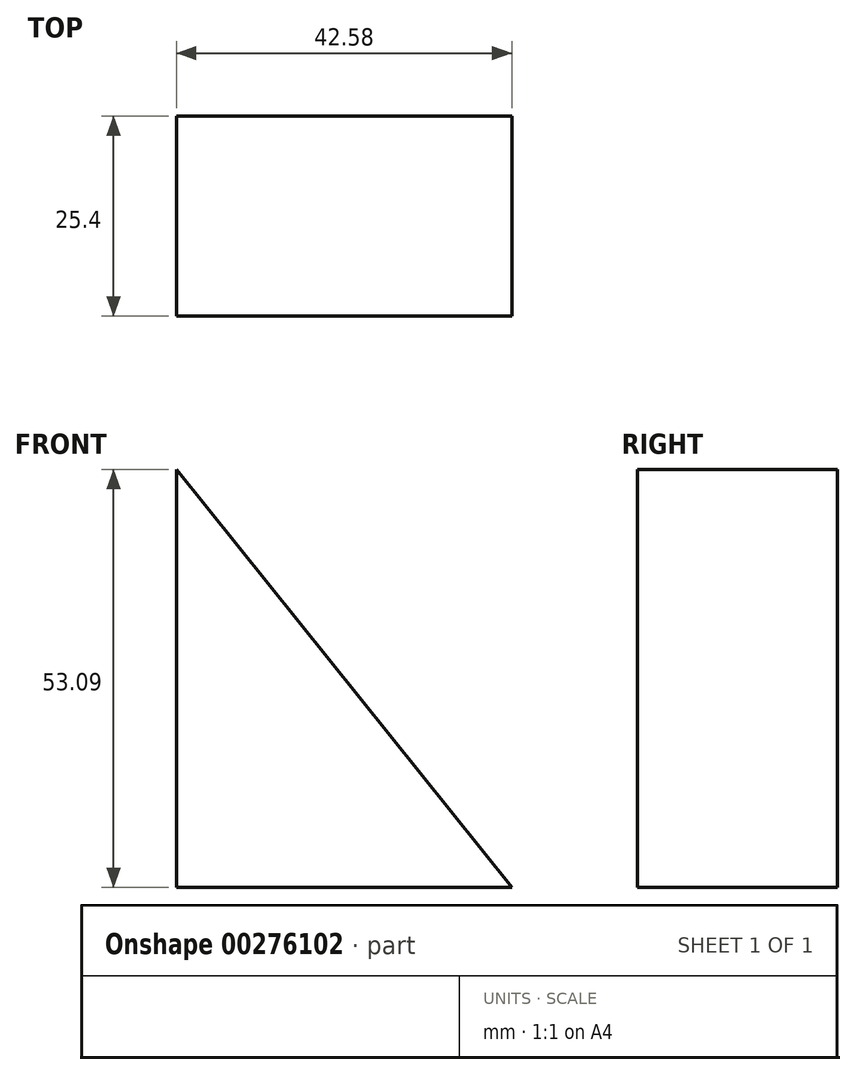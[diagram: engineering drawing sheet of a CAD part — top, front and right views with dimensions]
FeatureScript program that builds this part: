
annotation { "Feature Type Name" : "Feature", "Feature Type Description" : "" }
export const myFeature = defineFeature(function(context is Context, id is Id, definition is map)
    precondition{}
    {
        {
            var Q0;
            Q0=qCreatedBy(makeId("Front.planeOp"),FACE);
            var sketch = newSketch(context, id + "F0", { "sketchPlane" : qUnion([Q0])});
            skLineSegment(sketch, "E0", {"start": v(-54.42, 53.09) * mm, "end": v(-54.42, 0) * mm});
            skLineSegment(sketch, "E1", {"start": v(-11.84, 0) * mm, "end": v(-54.42, 53.09) * mm});
            skLineSegment(sketch, "E2", {"start": v(-54.42, 0) * mm, "end": v(-11.84, 0) * mm});
            skSolve(sketch);
        }
        {
            var Q0;
            Q0 = qSketchRegion(id + "F0", true);
            extrude(context, id + "F1", {"entities" : qUnion([Q0]), "depth" : 25.4 * mm});
        }
    });
